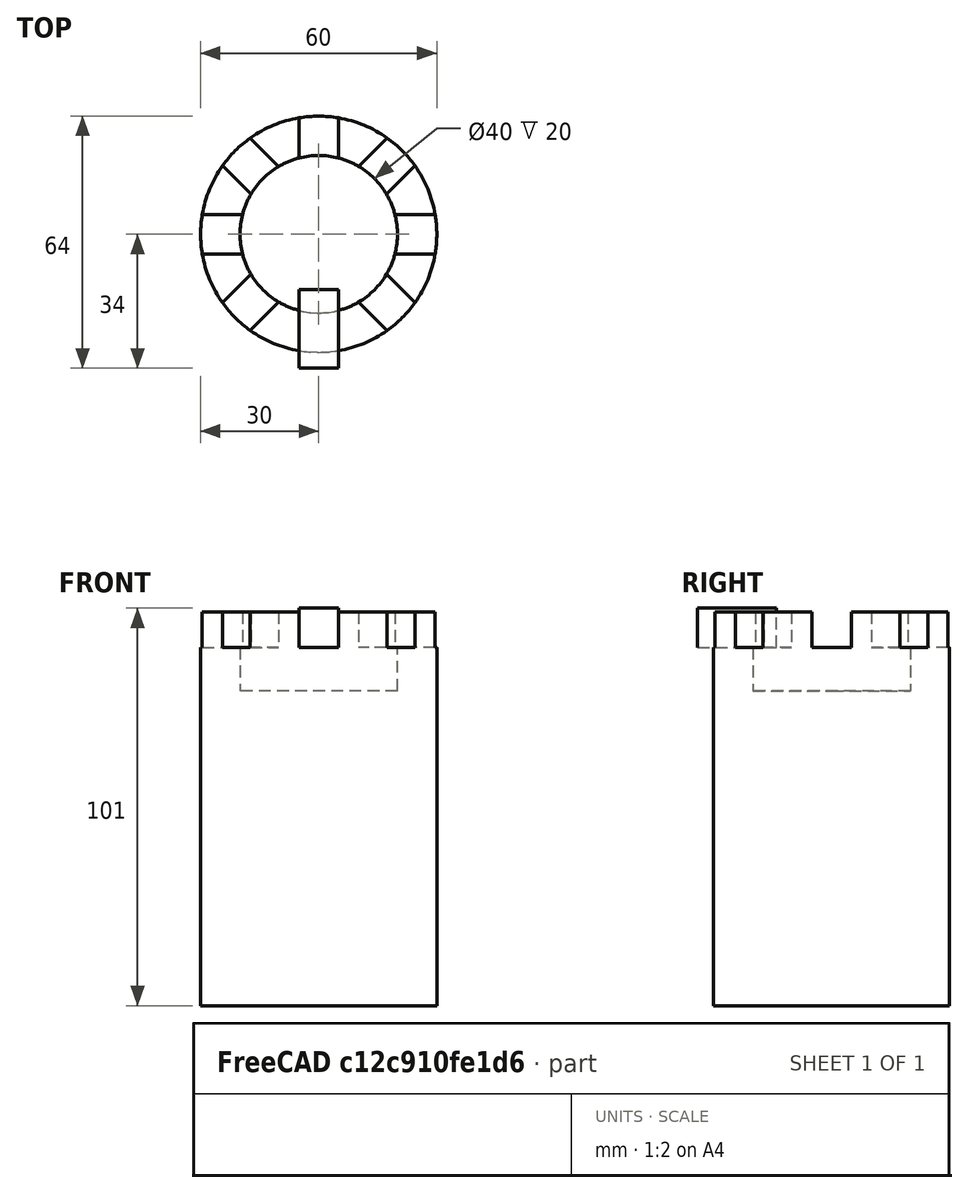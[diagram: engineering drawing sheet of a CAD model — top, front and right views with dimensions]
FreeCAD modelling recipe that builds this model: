
FCSTD DOCUMENT  (FreeCAD 0.20R29603 (Git))
Label: OJT1_T04R09_torre
License: All rights reserved
LicenseURL: http://en.wikipedia.org/wiki/All_rights_reserved
objects: Part::Cylinder×2, Part::Cut×2, Part::Box×1, Part::FeaturePython×1
note: 5 computed .brp shape members not serialized (recipe doc carries the construction recipe); baked Part::Feature solids carry a one-line shape summary decoded from their .brp

FEATURE [Part::Cylinder] Cylinder  label="Cilindre"
  Angle = 360
  AttacherType = Attacher::AttachEngine3D
  FirstAngle = 0
  Height = 100
  Radius = 30
  SecondAngle = 0
FEATURE [Part::Cylinder] Cylinder001  label="Cilindre001"
  Angle = 360
  AttacherType = Attacher::AttachEngine3D
  FirstAngle = 0
  Height = 20
  Placement = pos=(0,0,80) rot=(0,0,1;0rad)
  Radius = 20
  SecondAngle = 0
FEATURE [Part::Cut] Cut  label="resta 1"
  Base = -> Cylinder
  Tool = -> Cylinder001
FEATURE [Part::Box] Box  label="Cub"
  AttacherType = Attacher::AttachEngine3D
  Height = 10
  Length = 10
  Placement = pos=(-5,-34,91) rot=(0,0,1;0rad)
  Width = 20
FEATURE [Part::FeaturePython] Array  label="resta 2"  # Draft array (typed FeaturePython)
  AlwaysSyncPlacement = false
  Angle = 360
  ArrayType = 1
  Axis = (0,0,1)
  Base = -> Box
  Center = (0,0,0)
  Count = 8
  ExpandArray = false
  Fuse = false
  IntervalAxis = (0,0,0)
  IntervalX = (50,0,0)
  IntervalY = (0,50,0)
  IntervalZ = (0,0,50)
  NumberCircles = 3
  NumberPolar = 8
  NumberX = 2
  NumberY = 2
  NumberZ = 1
  PlacementList = 8 placements: [(-5,-34,91),(20.5061,-27.5772,91),(34,-5,91),(27.5772,20.5061,91),(5,34,91),(-20.5061,27.5772,91),(-34,5,91),(-27.5772,-20.5061,91)]
  RadialDistance = 50
  ScaleList = (8) [(1,1,1),(1,1,1),(1,1,1),(1,1,1),(1,1,1),(1,1,1),(1,1,1),(1,1,1)]
  Symmetry = 1
  TangentialDistance = 25
FEATURE [Part::Cut] Cut001  label="Torre"
  Base = -> Cut
  Tool = -> Array
